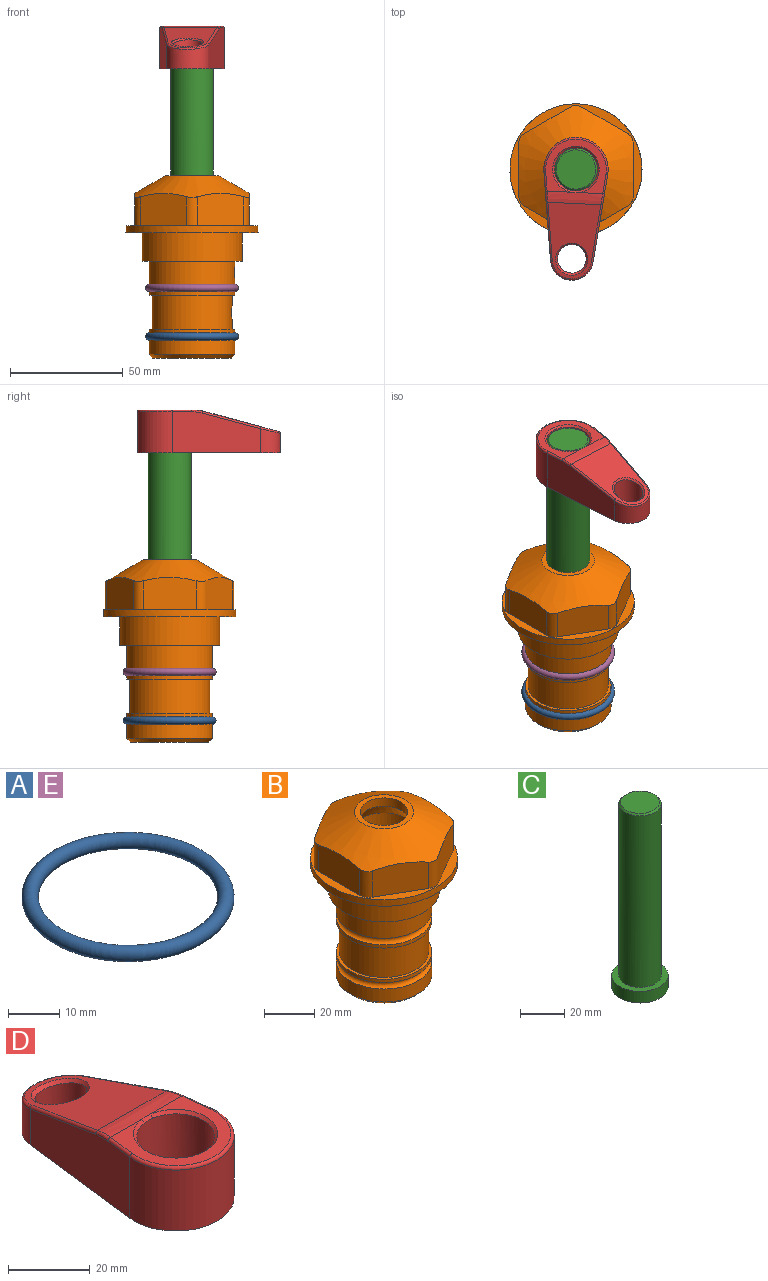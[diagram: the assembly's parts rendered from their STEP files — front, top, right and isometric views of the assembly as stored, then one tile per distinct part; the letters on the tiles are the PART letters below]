
ASSEMBLY  parts=5 mates=4
PART A: 1 faces, bbox 44.7x44.7x3.2 mm
  f0: torus R=19.05mm, axis (0,0,1), area 1193.9mm2
PART B: 36 faces, bbox 58.7x58.7x81 mm
  f0: cylinder r=17.78mm len=35.56mm, axis (0,0,1), area 1670.8mm2, adj f23,f24,f31
  f1: cylinder r=19.05mm len=38.1mm, axis (0,0,1), area 1191.9mm2, adj f26,f27,f30
  f2: plane 58.66x58.66mm, normal (0,0,-1), area 1150.6mm2, adj f3,f28
  f3: cylinder r=29.33mm len=58.66mm, axis (0,0,-1), area 585.1mm2, adj f2,f4
  f4: plane 58.66x58.66mm, normal (0,0,1), area 475.9mm2, adj f3,f5,f6,f7,f8,f9,f10,f11
  f5: plane 20.32x14.34mm, normal (-0.5,0.87,0), area 324.4mm2, adj f4,f15,f16,f17
  f6: plane 20.32x14.34mm, normal (0.5,0.87,0), area 324.4mm2, adj f4,f14,f15,f17
  f7: plane 23.48x14.34mm, normal (1,0,0), area 324.4mm2, adj f4,f13,f14,f17
  f8: plane 20.32x14.34mm, normal (0.5,-0.87,0), area 324.4mm2, adj f4,f12,f13,f17
  f9: plane 20.32x14.34mm, normal (-0.5,-0.87,0), area 324.4mm2, adj f4,f11,f12,f17
  f10: plane 23.48x14.34mm, normal (-1,0,0), area 324.4mm2, adj f4,f11,f16,f17
  f11: cylinder r=5.08mm len=12.85mm, axis (0,0,-1), area 67.2mm2, adj f4,f9,f10,f17
  f12: cylinder r=5.08mm len=12.85mm, axis (0,0,-1), area 67.2mm2, adj f4,f8,f9,f17
  f13: cylinder r=5.08mm len=12.85mm, axis (0,0,-1), area 67.2mm2, adj f4,f7,f8,f17
  f14: cylinder r=5.08mm len=12.85mm, axis (0,0,-1), area 67.2mm2, adj f4,f6,f7,f17
  f15: cylinder r=5.08mm len=12.85mm, axis (0,0,-1), area 67.2mm2, adj f4,f5,f6,f17
  f16: cylinder r=5.08mm len=12.85mm, axis (0,0,-1), area 67.2mm2, adj f4,f5,f10,f17
  f17: cone r=11.73mm half-angle=60deg, axis (0,0,-1), area 2071.8mm2, adj f5,f6,f7,f8,f9,f10,f11,f12
  f18: plane 23.46x23.46mm, normal (0,0,1), area 147.4mm2, adj f17,f35
  f19: plane 34.93x34.93mm, normal (0,0,-1), area 958mm2, adj f29
  f20: cylinder r=19.05mm len=38.1mm, axis (0,0,1), area 760.1mm2, adj f21,f29
  f21: torus R=19.05mm, axis (0,0,1), area 565.3mm2, adj f20,f22
  f22: cylinder r=19.05mm len=38.1mm, axis (0,0,1), area 190mm2, adj f21,f23
  f23: plane 38.1x38.1mm, normal (0,0,1), area 146.9mm2, adj f0,f22
  f24: plane 38.1x38.1mm, normal (0,0,-1), area 146.9mm2, adj f0,f25
  f25: cylinder r=19.05mm len=38.1mm, axis (0,0,1), area 190mm2, adj f24,f26
  f26: torus R=19.05mm, axis (0,0,1), area 565.3mm2, adj f1,f25
  f27: plane 44.45x44.45mm, normal (0,0,-1), area 411.7mm2, adj f1,f28
  f28: cylinder r=22.23mm len=44.45mm, axis (0,0,1), area 1773.5mm2, adj f2,f27
  f29: cone r=19.05mm half-angle=45deg, axis (0,0,1), area 257.5mm2, adj f19,f20
  f30: cylinder r=3.17mm len=6.75mm, axis (-1,0,0), area 128mm2, adj f1,f33
  f31: cylinder r=3.17mm len=6.35mm, axis (-1,0,0), area 102.5mm2, adj f0,f33
  f32: plane 25.4x25.4mm, normal (0,0,1), area 506.7mm2, adj f33
  f33: cylinder r=12.7mm len=66.42mm, axis (0,0,-1), area 5236.2mm2, adj f30,f31,f32,f34
  f34: cone r=9.53mm half-angle=30deg, axis (0,0,-1), area 443.4mm2, adj f33,f35
  f35: cylinder r=9.53mm len=19.05mm, axis (0,0,-1), area 240.9mm2, adj f18,f34
PART C: 6 faces, bbox 25.4x25.4x101.6 mm
  f0: plane 17.46x17.46mm, normal (0,0,1), area 239.5mm2, adj f5
  f1: plane 25.4x25.4mm, normal (0,0,-1), area 506.7mm2, adj f2
  f2: cylinder r=12.7mm len=25.4mm, axis (0,0,1), area 506.7mm2, adj f1,f3
  f3: plane 25.4x25.4mm, normal (0,0,1), area 221.7mm2, adj f2,f4
  f4: cylinder r=9.53mm len=94.46mm, axis (0,0,1), area 5653mm2, adj f3,f5
  f5: cone r=8.73mm half-angle=45deg, axis (0,0,-1), area 64.4mm2, adj f0,f4
PART D: 31 faces, bbox 31.7x65.5x19.8 mm
  f0: plane 39.12x18.26mm, normal (0.99,0.12,0), area 612.2mm2, adj f1,f4,f7,f11,f13,f15
  f1: cylinder r=9.53mm len=18.91mm, axis (0,0,-1), area 296.1mm2, adj f0,f2,f7,f17
  f2: plane 39.12x18.26mm, normal (-0.99,0.12,0), area 612.2mm2, adj f1,f4,f7,f12,f14,f16
  f3: cylinder r=6.35mm len=12.7mm, axis (0,0,-1), area 362.4mm2, adj f7,f18
  f4: cylinder r=14.29mm len=28.58mm, axis (0,0,-1), area 882.2mm2, adj f0,f2,f7,f10
  f5: cylinder r=9.53mm len=19.05mm, axis (0,0,-1), area 1092.6mm2, adj f7,f19,f20
  f6: plane 26.99x23.69mm, normal (0,0,1), area 216.2mm2, adj f9,f10,f11,f12,f19
  f7: plane 63.5x28.58mm, normal (0,0,-1), area 661.8mm2, adj f0,f1,f2,f3,f4,f5,f22,f23
  f8: plane 33.52x23.6mm, normal (0,0.26,0.97), area 486mm2, adj f9,f15,f16,f17,f18
  f9: cylinder r=19.05mm len=24.72mm, axis (1,0,0), area 120.4mm2, adj f6,f8,f13,f14,f20
  f10: torus R=13.49mm, axis (0,0,1), area 59mm2, adj f4,f6,f11,f12
  f11: cylinder r=0.79mm len=8.67mm, axis (0.12,-0.99,0), area 10.8mm2, adj f0,f6,f10,f13
  f12: cylinder r=0.79mm len=8.67mm, axis (0.12,0.99,0), area 10.8mm2, adj f2,f6,f10,f14
  f13: bspline ~4.95x1.42mm, area 6.1mm2, adj f0,f9,f11,f15
  f14: bspline ~4.95x1.42mm, area 6.1mm2, adj f2,f9,f12,f16
  f15: cylinder r=0.79mm len=25.95mm, axis (0.12,-0.96,0.26), area 32.9mm2, adj f0,f8,f13,f17
  f16: cylinder r=0.79mm len=25.95mm, axis (0.12,0.96,-0.26), area 32.9mm2, adj f2,f8,f14,f17
  f17: bspline ~18.91x8.38mm, area 30mm2, adj f1,f8,f15,f16
  f18: bspline ~14.29x14.29mm, area 48.3mm2, adj f3,f8
  f19: cone r=9.53mm half-angle=45deg, axis (0,0,1), area 66.5mm2, adj f5,f6,f20
  f20: bspline ~3.22x0.96mm, area 3.5mm2, adj f5,f9,f19
  f21: plane 2.75x2.72mm, normal (0,0,-1), area 2.9mm2, adj f23,f25,f28
  f22: plane 23.05x15.88mm, normal (-0.99,-0.12,0), area 323.6mm2, adj f7,f25,f26,f27,f28,f29
  f23: plane 23.05x15.88mm, normal (0.99,-0.12,0), area 323.6mm2, adj f7,f21,f25,f27,f28,f30
  f24: cylinder r=9.53mm len=10.69mm, axis (0,0,-1), area 114.7mm2, adj f7,f27,f29,f30
  f25: cylinder r=12.7mm len=20.59mm, axis (0,0,-1), area 381.1mm2, adj f7,f21,f22,f23,f26,f28
  f26: plane 2.75x2.72mm, normal (0,0,-1), area 2.9mm2, adj f22,f25,f28
  f27: plane 19.72x18.37mm, normal (0,-0.26,-0.97), area 291.8mm2, adj f22,f23,f24,f28,f29,f30
  f28: cylinder r=15.88mm len=19.92mm, axis (1,0,0), area 54.8mm2, adj f21,f22,f23,f25,f26,f27
  f29: cylinder r=1.59mm len=11mm, axis (0,0,-1), area 34.7mm2, adj f7,f22,f24,f27
  f30: cylinder r=1.59mm len=11mm, axis (0,0,-1), area 34.7mm2, adj f7,f23,f24,f27
PART E: same geometry as A
PLACE A t=(0,0,-21.59)mm
PLACE B at identity fixed
PLACE C rot(axis=(0,0,1),177.3deg) t=(0,0,27.55)mm
PLACE D rot(axis=(0,0,1),177.3deg) t=(0,0,28.35)mm
PLACE E at identity
MATE fastened A.f0 <-> B.f0  axis (0,0,1) through (0,0,-46.1)mm
MATE fastened E.f0 <-> B.f0  axis (0,0,1) through (0,0,-24.51)mm
MATE fastened D.f4 <-> C.f2  axis (0,0,-1) through (0,0,91.05)mm
MATE cylindrical C.f2 <-> B.f0  axis (0,0,-1) through (0,0,-10.55)mm
